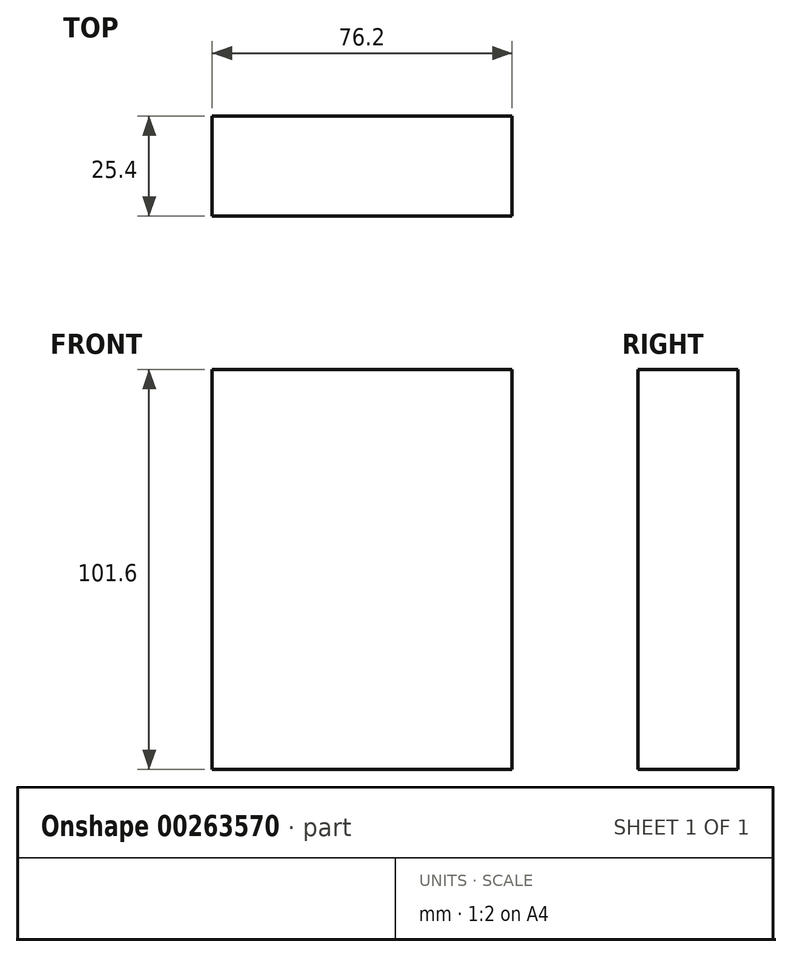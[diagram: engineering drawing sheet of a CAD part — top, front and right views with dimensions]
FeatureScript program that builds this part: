
annotation { "Feature Type Name" : "Feature", "Feature Type Description" : "" }
export const myFeature = defineFeature(function(context is Context, id is Id, definition is map)
    precondition{}
    {
        {
            var Q0;
            Q0=qCreatedBy(makeId("Front.planeOp"),FACE);
            var sketch = newSketch(context, id + "F0", { "sketchPlane" : qUnion([Q0])});
            skLineSegment(sketch, "E0.bottom", {"start": v(-2.16, 96.63) * mm, "end": v(74.04, 96.63) * mm});
            skLineSegment(sketch, "E0.top", {"start": v(-2.16, -4.97) * mm, "end": v(74.04, -4.97) * mm});
            skLineSegment(sketch, "E0.left", {"start": v(-2.16, 96.63) * mm, "end": v(-2.16, -4.97) * mm});
            skLineSegment(sketch, "E0.right", {"start": v(74.04, 96.63) * mm, "end": v(74.04, -4.97) * mm});
            skSolve(sketch);
        }
        {
            var Q0;
            Q0=makeQuery(id+"F0.imprint","IMPRINT",FACE,{"disambiguationData":[TD([[makeQuery(id+"F0.imprint","IMPRINT",EDGE,{"derivedFrom":sQuery(id+"F0.wireOp",EDGE,"E0.bottom")}),-1.0]])]});
            extrude(context, id + "F1", {"entities" : qUnion([Q0]), "oppositeDirection" : true, "depth" : 50.8 * mm});
        }
        {
            var Q0;
            Q0=makeQuery(id+"F1.opExtrude","CAP_FACE",FACE,{"disambiguationData":[OSD([sQuery(id+"F0.wireOp",EDGE,"E0.bottom"),sQuery(id+"F0.wireOp",EDGE,"E0.top"),sQuery(id+"F0.wireOp",EDGE,"E0.left"),sQuery(id+"F0.wireOp",EDGE,"E0.right")])],"isStart":false});
            var sketch = newSketch(context, id + "F2", { "sketchPlane" : qUnion([Q0])});
            skCircle(sketch, "E1", {"center": v(-27.12, 34.42) * mm, "radius": 16 * mm});
            skCircle(sketch, "E2", {"center": v(-27.12, 34.42) * mm, "radius": 1.77 * mm});
            skCircle(sketch, "E3", {"center": v(-42.14, 45.18) * mm, "radius": 4.97 * mm});
            skCircle(sketch, "E4", {"center": v(-30.39, 45.18) * mm, "radius": 28.34 * mm});
            skSolve(sketch);
        }
        {
            var Q0;
            Q0=makeQuery(id+"F2.imprint","IMPRINT",FACE,{"disambiguationData":[TD([[makeQuery(id+"F2.imprint","IMPRINT",EDGE,{"derivedFrom":sQuery(id+"F2.wireOp",EDGE,"E4")}),1.0]])]});
            var Q1;
            Q1=makeQuery(id+"F2.imprint","IMPRINT",FACE,{"disambiguationData":[TD([[makeQuery(id+"F2.imprint","IMPRINT",EDGE,{"derivedFrom":sQuery(id+"F2.wireOp",EDGE,"E2")}),-1.0]])]});
            var Q2;
            Q2=makeQuery(id+"F1.opExtrude","CAP_FACE",FACE,{"disambiguationData":[OSD([sQuery(id+"F0.wireOp",EDGE,"E0.bottom"),sQuery(id+"F0.wireOp",EDGE,"E0.top"),sQuery(id+"F0.wireOp",EDGE,"E0.left"),sQuery(id+"F0.wireOp",EDGE,"E0.right")])],"isStart":false});
            var Q3;
            Q3=makeQuery(id+"F1.opExtrude","CAP_FACE",FACE,{"disambiguationData":[OSD([sQuery(id+"F0.wireOp",EDGE,"E0.bottom"),sQuery(id+"F0.wireOp",EDGE,"E0.top"),sQuery(id+"F0.wireOp",EDGE,"E0.left"),sQuery(id+"F0.wireOp",EDGE,"E0.right")])],"isStart":true});
            extrude(context, id + "F3", {"entities" : qUnion([Q0, Q1, Q2, Q3]), "operationType" : NewBodyOperationType.REMOVE, "oppositeDirection" : true, "depth" : 25.4 * mm});
        }
    });
